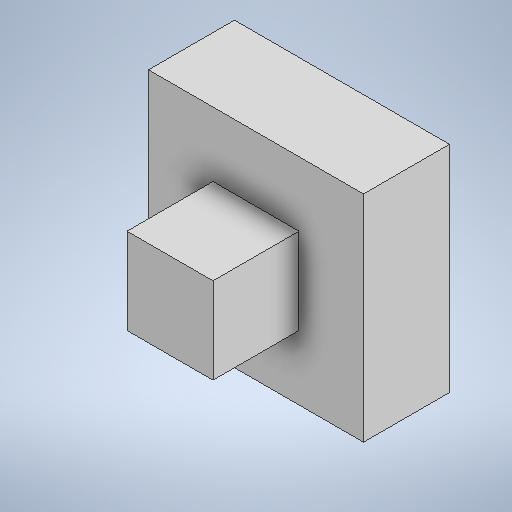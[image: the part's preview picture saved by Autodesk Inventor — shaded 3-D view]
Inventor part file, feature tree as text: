
AUTODESK INVENTOR PART (.ipt)
format: ipt  version: 2025.1 (Build 291241020, 241B)  size: 222,720 bytes
history: native  units: in
note: dims shown in document units (in); Inventor stores cm internally (conversion verified against a paired STEP export)
features: extrude x2, sketch x2
ambient origin geometry x8: Origin, YZ Plane, XZ Plane, XY Plane, X Axis, Y Axis, Z Axis, Center Point
bodies: Solid1 (feature_tree)
feature tree (4):
  extrude  "Extrusion1"  Depth=0.5in
  extrude  "Extrusion3"  Depth=0.15in
  sketch  "Sketch1"  dims[d0=0.5in d1=0.5in]
  sketch  "Sketch3"  dims[d2=0.2in d3=0.0in d10=0.15in d11=0.15in d12=0.15in d13=0.15in d14=0.2in d15=0.0in]
